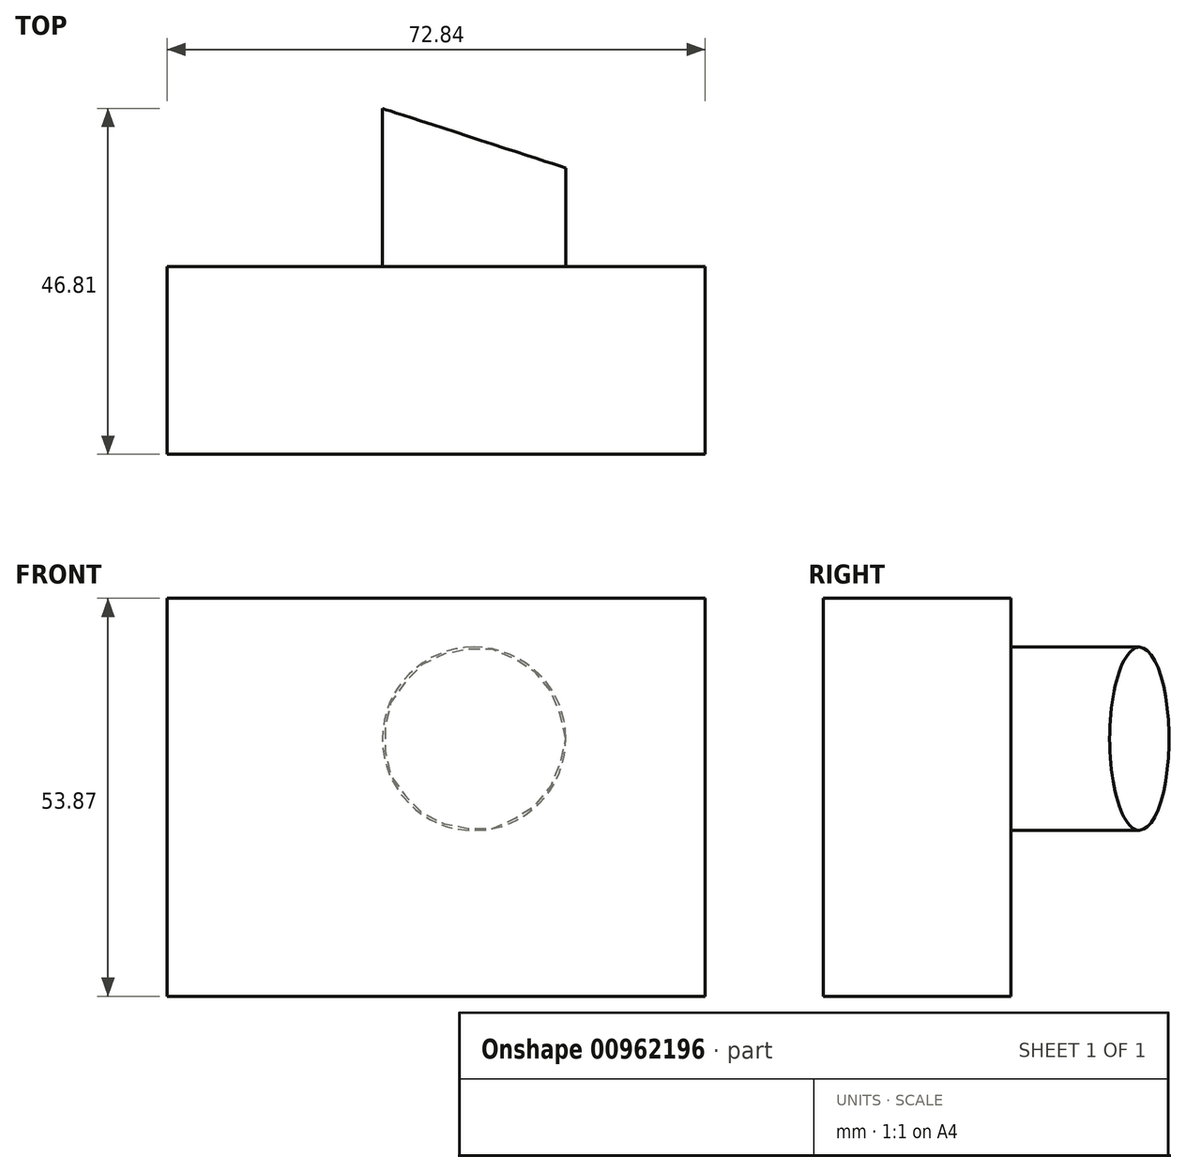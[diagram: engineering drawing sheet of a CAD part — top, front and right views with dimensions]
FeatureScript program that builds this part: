
annotation { "Feature Type Name" : "Feature", "Feature Type Description" : "" }
export const myFeature = defineFeature(function(context is Context, id is Id, definition is map)
    precondition{}
    {
        {
            var Q0;
            Q0=qCreatedBy(makeId("Front.planeOp"),FACE);
            var sketch = newSketch(context, id + "F0", { "sketchPlane" : qUnion([Q0])});
            skLineSegment(sketch, "E0.bottom", {"start": v(0, 0) * mm, "end": v(72.84, 0) * mm});
            skLineSegment(sketch, "E0.top", {"start": v(0, -53.87) * mm, "end": v(72.84, -53.87) * mm});
            skLineSegment(sketch, "E0.left", {"start": v(0, 0) * mm, "end": v(0, -53.87) * mm});
            skLineSegment(sketch, "E0.right", {"start": v(72.84, 0) * mm, "end": v(72.84, -53.87) * mm});
            skSolve(sketch);
        }
        {
            var Q0;
            Q0=qSketchRegion(id+"F0",true);
            var Q1;
            Q1=makeQuery(id+"F0.imprint","IMPRINT",FACE,{"disambiguationData":[TD([[makeQuery(id+"F0.imprint","IMPRINT",EDGE,{"derivedFrom":sQuery(id+"F0.wireOp",EDGE,"E0.bottom")}),-1.0]])]});
            extrude(context, id + "F1", {"entities" : qUnion([Q0, Q1]), "depth" : 25.4 * mm, "offsetDistance" : 25.4 * mm});
        }
        {
            var Q0;
            Q0=makeQuery(id+"F1.opExtrude","CAP_FACE",FACE,{"disambiguationData":[OSD([sQuery(id+"F0.wireOp",EDGE,"E0.bottom"),sQuery(id+"F0.wireOp",EDGE,"E0.top"),sQuery(id+"F0.wireOp",EDGE,"E0.left"),sQuery(id+"F0.wireOp",EDGE,"E0.right")])],"isStart":true});
            var sketch = newSketch(context, id + "F2", { "sketchPlane" : qUnion([Q0])});
            skCircle(sketch, "E1", {"center": v(-41.56, -19.03) * mm, "radius": 12.42 * mm});
            skSolve(sketch);
        }
        {
            var Q0;
            Q0=makeQuery(id+"F2.imprint","IMPRINT",FACE,{"disambiguationData":[TD([[makeQuery(id+"F2.imprint","IMPRINT",EDGE,{"derivedFrom":sQuery(id+"F2.wireOp",EDGE,"E1")}),1.0]])]});
            extrude(context, id + "F3", {"entities" : qUnion([Q0]), "operationType" : NewBodyOperationType.ADD, "depth" : 25.4 * mm, "offsetDistance" : 25.4 * mm});
        }
        {
            var Q0;
            Q0=qCreatedBy(makeId("Top.planeOp"),FACE);
            var sketch = newSketch(context, id + "F4", { "sketchPlane" : qUnion([Q0])});
            skLineSegment(sketch, "E2", {"start": v(18.42, 24.9) * mm, "end": v(61.88, 10.8) * mm});
            skLineSegment(sketch, "E3", {"start": v(61.88, 10.8) * mm, "end": v(61.88, 30.36) * mm});
            skLineSegment(sketch, "E4", {"start": v(61.88, 30.36) * mm, "end": v(18.42, 24.9) * mm});
            skSolve(sketch);
        }
        {
            var Q0;
            Q0=makeQuery(id+"F4.imprint","IMPRINT",FACE,{"disambiguationData":[TD([[makeQuery(id+"F4.imprint","IMPRINT",EDGE,{"derivedFrom":sQuery(id+"F4.wireOp",EDGE,"E2")}),1.0]])]});
            extrude(context, id + "F5", {"entities" : qUnion([Q0]), "operationType" : NewBodyOperationType.REMOVE, "oppositeDirection" : true, "depth" : 40.13 * mm, "offsetDistance" : 25.4 * mm});
        }
    });
